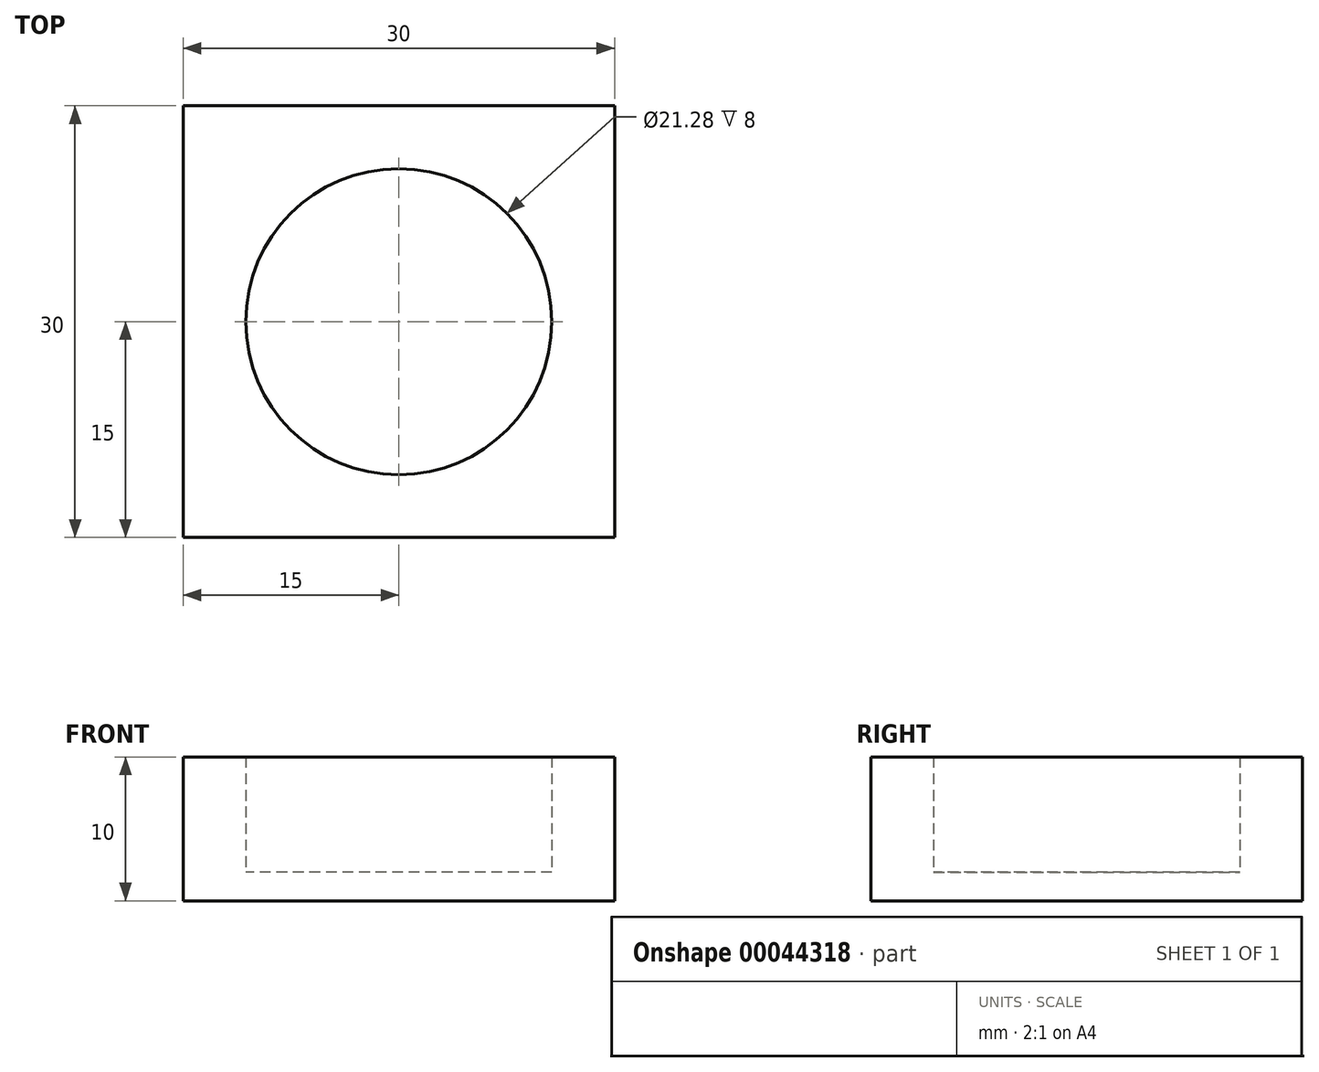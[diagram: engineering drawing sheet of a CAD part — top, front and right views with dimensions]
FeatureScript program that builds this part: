
annotation { "Feature Type Name" : "Feature", "Feature Type Description" : "" }
export const myFeature = defineFeature(function(context is Context, id is Id, definition is map)
    precondition{}
    {
        {
            var Q0;
            Q0=qCreatedBy(makeId("Top.planeOp"),FACE);
            var sketch = newSketch(context, id + "F0", { "sketchPlane" : qUnion([Q0])});
            skCircle(sketch, "E0", {"center": v(0, 0) * mm, "radius": 10.64 * mm});
            skLineSegment(sketch, "E1.bottom", {"start": v(15, -15) * mm, "end": v(-15, -15) * mm});
            skLineSegment(sketch, "E1.top", {"start": v(15, 15) * mm, "end": v(-15, 15) * mm});
            skLineSegment(sketch, "E1.left", {"start": v(15, -15) * mm, "end": v(15, 15) * mm});
            skLineSegment(sketch, "E1.right", {"start": v(-15, -15) * mm, "end": v(-15, 15) * mm});
            skSolve(sketch);
        }
        {
            var Q0;
            Q0 = qSketchRegion(id + "F0", true);
            extrude(context, id + "F1", {"entities" : qUnion([Q0]), "depth" : 10 * mm});
        }
        {
            var Q0;
            Q0=makeQuery(id+"F0.imprint","IMPRINT",FACE,{"disambiguationData":[TD([[makeQuery(id+"F0.imprint","IMPRINT",EDGE,{"derivedFrom":sQuery(id+"F0.wireOp",EDGE,"E0")}),1.0]])]});
            extrude(context, id + "F2", {"entities" : qUnion([Q0]), "operationType" : NewBodyOperationType.ADD, "depth" : 2 * mm});
        }
    });
